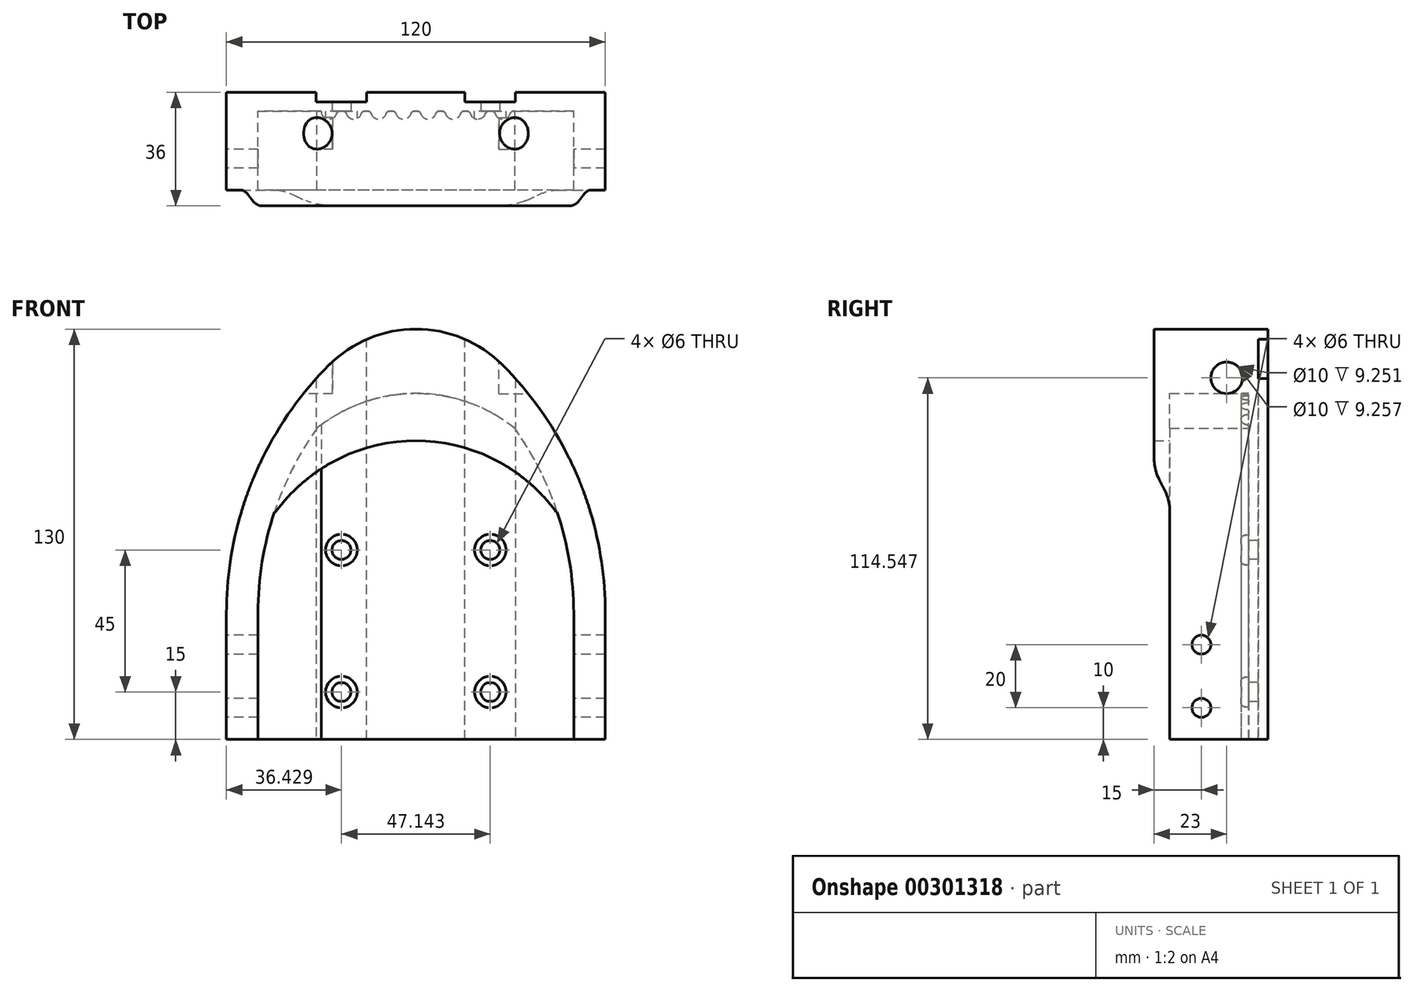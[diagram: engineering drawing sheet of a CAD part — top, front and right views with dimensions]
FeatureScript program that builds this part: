
annotation { "Feature Type Name" : "Feature", "Feature Type Description" : "" }
export const myFeature = defineFeature(function(context is Context, id is Id, definition is map)
    precondition{}
    {
        {
            var Q0;
            Q0=qCreatedBy(makeId("Front.planeOp"),FACE);
            var sketch = newSketch(context, id + "F0", { "sketchPlane" : qUnion([Q0])});
            skArc(sketch, "E0", {"start": v(-27.5, 118.6) * mm, "mid": v(-51.55, 82.52) * mm, "end": v(-60, 40) * mm});
            skArc(sketch, "E1", {"start": v(0, 130) * mm, "mid": v(-14.89, 127.03) * mm, "end": v(-27.5, 118.6) * mm});
            skLineSegment(sketch, "E2", {"start": v(-60, 0) * mm, "end": v(0, 0) * mm});
            skArc(sketch, "E3.MirrorCS", {"start": v(0, 130) * mm, "mid": v(14.89, 127.03) * mm, "end": v(27.5, 118.6) * mm});
            skArc(sketch, "E4.MirrorCS", {"start": v(27.5, 118.6) * mm, "mid": v(51.55, 82.52) * mm, "end": v(60, 40) * mm});
            skLineSegment(sketch, "E5.MirrorCS", {"start": v(60, 0) * mm, "end": v(0, 0) * mm});
            skLineSegment(sketch, "E6", {"start": v(-60, 40) * mm, "end": v(-60, 0) * mm});
            skLineSegment(sketch, "E7", {"start": v(60, 40) * mm, "end": v(60, 0) * mm});
            skSolve(sketch);
        }
        {
            var Q0;
            Q0=qSketchRegion(id+"F0",true);
            extrude(context, id + "F1", {"entities" : qUnion([Q0]), "depth" : 3 * mm});
        }
        {
            var Q0;
            Q0=makeQuery(id+"F1.opExtrude","CAP_FACE",FACE,{"disambiguationData":[OSD([sQuery(id+"F0.wireOp",EDGE,"E0"),sQuery(id+"F0.wireOp",EDGE,"E1"),sQuery(id+"F0.wireOp",EDGE,"E2"),sQuery(id+"F0.wireOp",EDGE,"E3.MirrorCS"),sQuery(id+"F0.wireOp",EDGE,"E4.MirrorCS"),sQuery(id+"F0.wireOp",EDGE,"E5.MirrorCS")])],"isStart":false});
            var sketch = newSketch(context, id + "F2", { "sketchPlane" : qUnion([Q0])});
            skArc(sketch, "E8", {"start": v(27.5, 118.6) * mm, "mid": v(0, 130) * mm, "end": v(-27.5, 118.6) * mm});
            skLineSegment(sketch, "E9", {"start": v(-27.5, 118.6) * mm, "end": v(-27.5, 118.6) * mm});
            skArc(sketch, "E10", {"start": v(0, 109.62) * mm, "mid": v(-16.6, 106.78) * mm, "end": v(-31.33, 98.6) * mm});
            skLineSegment(sketch, "E11", {"start": v(-50, 0) * mm, "end": v(-60, 0) * mm});
            skArc(sketch, "E12", {"start": v(-27.5, 118.6) * mm, "mid": v(-51.55, 82.52) * mm, "end": v(-60, 40) * mm});
            skLineSegment(sketch, "E13", {"start": v(-60, 40) * mm, "end": v(-60, 0) * mm});
            skLineSegment(sketch, "E14", {"start": v(-50, 0) * mm, "end": v(-50, 40) * mm});
            skArc(sketch, "E15", {"start": v(-31.33, 98.6) * mm, "mid": v(-45.22, 70.75) * mm, "end": v(-50, 40) * mm});
            skArc(sketch, "E16.MirrorCS", {"start": v(27.5, 118.6) * mm, "mid": v(51.55, 82.52) * mm, "end": v(60, 40) * mm});
            skLineSegment(sketch, "E17.MirrorCS", {"start": v(50, 0) * mm, "end": v(60, 0) * mm});
            skArc(sketch, "E18.MirrorCS", {"start": v(31.33, 98.6) * mm, "mid": v(45.22, 70.75) * mm, "end": v(50, 40) * mm});
            skLineSegment(sketch, "E19.MirrorCS", {"start": v(50, 0) * mm, "end": v(50, 40) * mm});
            skLineSegment(sketch, "E20.MirrorCS", {"start": v(60, 40) * mm, "end": v(60, 0) * mm});
            skArc(sketch, "E21.MirrorCS", {"start": v(0, 109.62) * mm, "mid": v(16.6, 106.78) * mm, "end": v(31.33, 98.6) * mm});
            skSolve(sketch);
        }
        {
            var Q0;
            Q0=qSketchRegion(id+"F2",true);
            extrude(context, id + "F3", {"entities" : qUnion([Q0]), "operationType" : NewBodyOperationType.ADD, "depth" : 25 * mm});
        }
        {
            var Q0;
            Q0=makeQuery(id+"F1.opExtrude","SWEPT_FACE",FACE,{"disambiguationData":[OSD([sQuery(id+"F0.wireOp",EDGE,"E2"),sQuery(id+"F0.wireOp",EDGE,"E5.MirrorCS")])]});
            var sketch = newSketch(context, id + "F4", { "sketchPlane" : qUnion([Q0])});
            skArc(sketch, "E22", {"start": v(30, 3) * mm, "mid": v(27.5, 5.5) * mm, "end": v(25, 3) * mm});
            skLineSegment(sketch, "E23", {"start": v(25, 3) * mm, "end": v(30, 3) * mm});
            skArc(sketch, "E24.1.0.0", {"start": v(22.14, 3) * mm, "mid": v(19.64, 5.5) * mm, "end": v(17.14, 3) * mm});
            skLineSegment(sketch, "E24.1.0.1", {"start": v(17.14, 3) * mm, "end": v(22.14, 3) * mm});
            skArc(sketch, "E24.2.0.0", {"start": v(14.29, 3) * mm, "mid": v(11.79, 5.5) * mm, "end": v(9.29, 3) * mm});
            skLineSegment(sketch, "E24.2.0.1", {"start": v(9.29, 3) * mm, "end": v(14.29, 3) * mm});
            skArc(sketch, "E24.3.0.0", {"start": v(6.43, 3) * mm, "mid": v(3.93, 5.5) * mm, "end": v(1.43, 3) * mm});
            skLineSegment(sketch, "E24.3.0.1", {"start": v(1.43, 3) * mm, "end": v(6.43, 3) * mm});
            skArc(sketch, "E24.4.0.0", {"start": v(-1.43, 3) * mm, "mid": v(-3.93, 5.5) * mm, "end": v(-6.43, 3) * mm});
            skLineSegment(sketch, "E24.4.0.1", {"start": v(-6.43, 3) * mm, "end": v(-1.43, 3) * mm});
            skArc(sketch, "E24.5.0.0", {"start": v(-9.29, 3) * mm, "mid": v(-11.79, 5.5) * mm, "end": v(-14.29, 3) * mm});
            skLineSegment(sketch, "E24.5.0.1", {"start": v(-14.29, 3) * mm, "end": v(-9.29, 3) * mm});
            skArc(sketch, "E24.6.0.0", {"start": v(-17.14, 3) * mm, "mid": v(-19.64, 5.5) * mm, "end": v(-22.14, 3) * mm});
            skLineSegment(sketch, "E24.6.0.1", {"start": v(-22.14, 3) * mm, "end": v(-17.14, 3) * mm});
            skArc(sketch, "E24.7.0.0", {"start": v(-25, 3) * mm, "mid": v(-27.5, 5.5) * mm, "end": v(-30, 3) * mm});
            skLineSegment(sketch, "E24.7.0.1", {"start": v(-30, 3) * mm, "end": v(-25, 3) * mm});
            skLineSegment(sketch, "E24.direction1", {"start": v(17.14, 3) * mm, "end": v(25, 3) * mm, "construction": true});
            skSolve(sketch);
        }
        {
            var Q0;
            Q0=qSketchRegion(id+"F4",true);
            extrude(context, id + "F5", {"entities" : qUnion([Q0]), "operationType" : NewBodyOperationType.ADD, "endBound" : BoundingType.UP_TO_NEXT, "oppositeDirection" : true, "depth" : 25 * mm});
        }
        {
            var Q0;
            {var subQ0=sQuery(id+"F4.wireOp",EDGE,"E23");var subQ1=sQuery(id+"F4.wireOp",EDGE,"E22");var subQ2=sQuery(id+"F0.wireOp",EDGE,"E5.MirrorCS");var subQ3=sQuery(id+"F0.wireOp",EDGE,"E2");Q0=makeQuery(id+"F5.opExtrude","SWEPT_EDGE",EDGE,{"disambiguationData":[OSD([subQ3,subQ2,subQ1,subQ0]),TDD([makeQuery(id+"F4.imprint","INTERSECT",VERTEX,{"disambiguationData":[OD(1.0)],"derivedFrom":[makeQuery(id+"F1.opExtrude","CAP_EDGE",EDGE,{"disambiguationData":[OSD([subQ3,subQ2])],"isStart":false}),subQ1,subQ0]})])]});}
            var Q1;
            {var subQ0=sQuery(id+"F4.wireOp",EDGE,"E23");var subQ1=sQuery(id+"F4.wireOp",EDGE,"E22");var subQ2=sQuery(id+"F0.wireOp",EDGE,"E5.MirrorCS");var subQ3=sQuery(id+"F0.wireOp",EDGE,"E2");Q1=makeQuery(id+"F5.opExtrude","SWEPT_EDGE",EDGE,{"disambiguationData":[OSD([subQ3,subQ2,subQ1,subQ0]),TDD([makeQuery(id+"F4.imprint","INTERSECT",VERTEX,{"disambiguationData":[OD(0.0)],"derivedFrom":[makeQuery(id+"F1.opExtrude","CAP_EDGE",EDGE,{"disambiguationData":[OSD([subQ3,subQ2])],"isStart":false}),subQ1,subQ0]})])]});}
            var Q2;
            {var subQ0=sQuery(id+"F4.wireOp",EDGE,"E24.1.0.1");var subQ1=sQuery(id+"F4.wireOp",EDGE,"E24.1.0.0");var subQ2=sQuery(id+"F0.wireOp",EDGE,"E5.MirrorCS");var subQ3=sQuery(id+"F0.wireOp",EDGE,"E2");Q2=makeQuery(id+"F5.opExtrude","SWEPT_EDGE",EDGE,{"disambiguationData":[OSD([subQ3,subQ2,subQ1,subQ0]),TDD([makeQuery(id+"F4.imprint","INTERSECT",VERTEX,{"disambiguationData":[OD(0.0)],"derivedFrom":[makeQuery(id+"F1.opExtrude","CAP_EDGE",EDGE,{"disambiguationData":[OSD([subQ3,subQ2])],"isStart":false}),subQ1,subQ0]})])]});}
            var Q3;
            {var subQ0=sQuery(id+"F4.wireOp",EDGE,"E24.2.0.1");var subQ1=sQuery(id+"F4.wireOp",EDGE,"E24.2.0.0");var subQ2=sQuery(id+"F0.wireOp",EDGE,"E5.MirrorCS");var subQ3=sQuery(id+"F0.wireOp",EDGE,"E2");Q3=makeQuery(id+"F5.opExtrude","SWEPT_EDGE",EDGE,{"disambiguationData":[OSD([subQ3,subQ2,subQ1,subQ0]),TDD([makeQuery(id+"F4.imprint","INTERSECT",VERTEX,{"disambiguationData":[OD(0.0)],"derivedFrom":[makeQuery(id+"F1.opExtrude","CAP_EDGE",EDGE,{"disambiguationData":[OSD([subQ3,subQ2])],"isStart":false}),subQ1,subQ0]})])]});}
            var Q4;
            {var subQ0=sQuery(id+"F4.wireOp",EDGE,"E24.3.0.1");var subQ1=sQuery(id+"F4.wireOp",EDGE,"E24.3.0.0");var subQ2=sQuery(id+"F0.wireOp",EDGE,"E5.MirrorCS");var subQ3=sQuery(id+"F0.wireOp",EDGE,"E2");Q4=makeQuery(id+"F5.opExtrude","SWEPT_EDGE",EDGE,{"disambiguationData":[OSD([subQ3,subQ2,subQ1,subQ0]),TDD([makeQuery(id+"F4.imprint","INTERSECT",VERTEX,{"disambiguationData":[OD(0.0)],"derivedFrom":[makeQuery(id+"F1.opExtrude","CAP_EDGE",EDGE,{"disambiguationData":[OSD([subQ3,subQ2])],"isStart":false}),subQ1,subQ0]})])]});}
            var Q5;
            {var subQ0=sQuery(id+"F4.wireOp",EDGE,"E24.4.0.1");var subQ1=sQuery(id+"F4.wireOp",EDGE,"E24.4.0.0");var subQ2=sQuery(id+"F0.wireOp",EDGE,"E5.MirrorCS");var subQ3=sQuery(id+"F0.wireOp",EDGE,"E2");Q5=makeQuery(id+"F5.opExtrude","SWEPT_EDGE",EDGE,{"disambiguationData":[OSD([subQ3,subQ2,subQ1,subQ0]),TDD([makeQuery(id+"F4.imprint","INTERSECT",VERTEX,{"disambiguationData":[OD(0.0)],"derivedFrom":[makeQuery(id+"F1.opExtrude","CAP_EDGE",EDGE,{"disambiguationData":[OSD([subQ3,subQ2])],"isStart":false}),subQ1,subQ0]})])]});}
            var Q6;
            {var subQ0=sQuery(id+"F4.wireOp",EDGE,"E24.5.0.1");var subQ1=sQuery(id+"F4.wireOp",EDGE,"E24.5.0.0");var subQ2=sQuery(id+"F0.wireOp",EDGE,"E5.MirrorCS");var subQ3=sQuery(id+"F0.wireOp",EDGE,"E2");Q6=makeQuery(id+"F5.opExtrude","SWEPT_EDGE",EDGE,{"disambiguationData":[OSD([subQ3,subQ2,subQ1,subQ0]),TDD([makeQuery(id+"F4.imprint","INTERSECT",VERTEX,{"disambiguationData":[OD(0.0)],"derivedFrom":[makeQuery(id+"F1.opExtrude","CAP_EDGE",EDGE,{"disambiguationData":[OSD([subQ3,subQ2])],"isStart":false}),subQ1,subQ0]})])]});}
            var Q7;
            {var subQ0=sQuery(id+"F4.wireOp",EDGE,"E24.6.0.1");var subQ1=sQuery(id+"F4.wireOp",EDGE,"E24.6.0.0");var subQ2=sQuery(id+"F0.wireOp",EDGE,"E5.MirrorCS");var subQ3=sQuery(id+"F0.wireOp",EDGE,"E2");Q7=makeQuery(id+"F5.opExtrude","SWEPT_EDGE",EDGE,{"disambiguationData":[OSD([subQ3,subQ2,subQ1,subQ0]),TDD([makeQuery(id+"F4.imprint","INTERSECT",VERTEX,{"disambiguationData":[OD(0.0)],"derivedFrom":[makeQuery(id+"F1.opExtrude","CAP_EDGE",EDGE,{"disambiguationData":[OSD([subQ3,subQ2])],"isStart":false}),subQ1,subQ0]})])]});}
            var Q8;
            {var subQ0=sQuery(id+"F4.wireOp",EDGE,"E24.7.0.1");var subQ1=sQuery(id+"F4.wireOp",EDGE,"E24.7.0.0");var subQ2=sQuery(id+"F0.wireOp",EDGE,"E5.MirrorCS");var subQ3=sQuery(id+"F0.wireOp",EDGE,"E2");Q8=makeQuery(id+"F5.opExtrude","SWEPT_EDGE",EDGE,{"disambiguationData":[OSD([subQ3,subQ2,subQ1,subQ0]),TDD([makeQuery(id+"F4.imprint","INTERSECT",VERTEX,{"disambiguationData":[OD(0.0)],"derivedFrom":[makeQuery(id+"F1.opExtrude","CAP_EDGE",EDGE,{"disambiguationData":[OSD([subQ3,subQ2])],"isStart":false}),subQ1,subQ0]})])]});}
            var Q9;
            {var subQ0=sQuery(id+"F4.wireOp",EDGE,"E24.8.0.1");var subQ1=sQuery(id+"F4.wireOp",EDGE,"E24.8.0.0");var subQ2=sQuery(id+"F0.wireOp",EDGE,"E5.MirrorCS");var subQ3=sQuery(id+"F0.wireOp",EDGE,"E2");Q9=makeQuery(id+"F5.opExtrude","SWEPT_EDGE",EDGE,{"disambiguationData":[OSD([subQ3,subQ2,subQ1,subQ0]),TDD([makeQuery(id+"F4.imprint","INTERSECT",VERTEX,{"disambiguationData":[OD(0.0)],"derivedFrom":[makeQuery(id+"F1.opExtrude","CAP_EDGE",EDGE,{"disambiguationData":[OSD([subQ3,subQ2])],"isStart":false}),subQ1,subQ0]})])]});}
            var Q10;
            {var subQ0=sQuery(id+"F4.wireOp",EDGE,"E24.9.0.1");var subQ1=sQuery(id+"F4.wireOp",EDGE,"E24.9.0.0");var subQ2=sQuery(id+"F0.wireOp",EDGE,"E5.MirrorCS");var subQ3=sQuery(id+"F0.wireOp",EDGE,"E2");Q10=makeQuery(id+"F5.opExtrude","SWEPT_EDGE",EDGE,{"disambiguationData":[OSD([subQ3,subQ2,subQ1,subQ0]),TDD([makeQuery(id+"F4.imprint","INTERSECT",VERTEX,{"disambiguationData":[OD(0.0)],"derivedFrom":[makeQuery(id+"F1.opExtrude","CAP_EDGE",EDGE,{"disambiguationData":[OSD([subQ3,subQ2])],"isStart":false}),subQ1,subQ0]})])]});}
            var Q11;
            {var subQ0=sQuery(id+"F4.wireOp",EDGE,"E24.1.0.1");var subQ1=sQuery(id+"F4.wireOp",EDGE,"E24.1.0.0");var subQ2=sQuery(id+"F0.wireOp",EDGE,"E5.MirrorCS");var subQ3=sQuery(id+"F0.wireOp",EDGE,"E2");Q11=makeQuery(id+"F5.opExtrude","SWEPT_EDGE",EDGE,{"disambiguationData":[OSD([subQ3,subQ2,subQ1,subQ0]),TDD([makeQuery(id+"F4.imprint","INTERSECT",VERTEX,{"disambiguationData":[OD(1.0)],"derivedFrom":[makeQuery(id+"F1.opExtrude","CAP_EDGE",EDGE,{"disambiguationData":[OSD([subQ3,subQ2])],"isStart":false}),subQ1,subQ0]})])]});}
            var Q12;
            {var subQ0=sQuery(id+"F4.wireOp",EDGE,"E24.2.0.1");var subQ1=sQuery(id+"F4.wireOp",EDGE,"E24.2.0.0");var subQ2=sQuery(id+"F0.wireOp",EDGE,"E5.MirrorCS");var subQ3=sQuery(id+"F0.wireOp",EDGE,"E2");Q12=makeQuery(id+"F5.opExtrude","SWEPT_EDGE",EDGE,{"disambiguationData":[OSD([subQ3,subQ2,subQ1,subQ0]),TDD([makeQuery(id+"F4.imprint","INTERSECT",VERTEX,{"disambiguationData":[OD(1.0)],"derivedFrom":[makeQuery(id+"F1.opExtrude","CAP_EDGE",EDGE,{"disambiguationData":[OSD([subQ3,subQ2])],"isStart":false}),subQ1,subQ0]})])]});}
            var Q13;
            {var subQ0=sQuery(id+"F4.wireOp",EDGE,"E24.3.0.1");var subQ1=sQuery(id+"F4.wireOp",EDGE,"E24.3.0.0");var subQ2=sQuery(id+"F0.wireOp",EDGE,"E5.MirrorCS");var subQ3=sQuery(id+"F0.wireOp",EDGE,"E2");Q13=makeQuery(id+"F5.opExtrude","SWEPT_EDGE",EDGE,{"disambiguationData":[OSD([subQ3,subQ2,subQ1,subQ0]),TDD([makeQuery(id+"F4.imprint","INTERSECT",VERTEX,{"disambiguationData":[OD(1.0)],"derivedFrom":[makeQuery(id+"F1.opExtrude","CAP_EDGE",EDGE,{"disambiguationData":[OSD([subQ3,subQ2])],"isStart":false}),subQ1,subQ0]})])]});}
            var Q14;
            {var subQ0=sQuery(id+"F4.wireOp",EDGE,"E24.4.0.1");var subQ1=sQuery(id+"F4.wireOp",EDGE,"E24.4.0.0");var subQ2=sQuery(id+"F0.wireOp",EDGE,"E5.MirrorCS");var subQ3=sQuery(id+"F0.wireOp",EDGE,"E2");Q14=makeQuery(id+"F5.opExtrude","SWEPT_EDGE",EDGE,{"disambiguationData":[OSD([subQ3,subQ2,subQ1,subQ0]),TDD([makeQuery(id+"F4.imprint","INTERSECT",VERTEX,{"disambiguationData":[OD(1.0)],"derivedFrom":[makeQuery(id+"F1.opExtrude","CAP_EDGE",EDGE,{"disambiguationData":[OSD([subQ3,subQ2])],"isStart":false}),subQ1,subQ0]})])]});}
            var Q15;
            {var subQ0=sQuery(id+"F4.wireOp",EDGE,"E24.5.0.1");var subQ1=sQuery(id+"F4.wireOp",EDGE,"E24.5.0.0");var subQ2=sQuery(id+"F0.wireOp",EDGE,"E5.MirrorCS");var subQ3=sQuery(id+"F0.wireOp",EDGE,"E2");Q15=makeQuery(id+"F5.opExtrude","SWEPT_EDGE",EDGE,{"disambiguationData":[OSD([subQ3,subQ2,subQ1,subQ0]),TDD([makeQuery(id+"F4.imprint","INTERSECT",VERTEX,{"disambiguationData":[OD(1.0)],"derivedFrom":[makeQuery(id+"F1.opExtrude","CAP_EDGE",EDGE,{"disambiguationData":[OSD([subQ3,subQ2])],"isStart":false}),subQ1,subQ0]})])]});}
            var Q16;
            {var subQ0=sQuery(id+"F4.wireOp",EDGE,"E24.6.0.1");var subQ1=sQuery(id+"F4.wireOp",EDGE,"E24.6.0.0");var subQ2=sQuery(id+"F0.wireOp",EDGE,"E5.MirrorCS");var subQ3=sQuery(id+"F0.wireOp",EDGE,"E2");Q16=makeQuery(id+"F5.opExtrude","SWEPT_EDGE",EDGE,{"disambiguationData":[OSD([subQ3,subQ2,subQ1,subQ0]),TDD([makeQuery(id+"F4.imprint","INTERSECT",VERTEX,{"disambiguationData":[OD(1.0)],"derivedFrom":[makeQuery(id+"F1.opExtrude","CAP_EDGE",EDGE,{"disambiguationData":[OSD([subQ3,subQ2])],"isStart":false}),subQ1,subQ0]})])]});}
            var Q17;
            {var subQ0=sQuery(id+"F4.wireOp",EDGE,"E24.7.0.1");var subQ1=sQuery(id+"F4.wireOp",EDGE,"E24.7.0.0");var subQ2=sQuery(id+"F0.wireOp",EDGE,"E5.MirrorCS");var subQ3=sQuery(id+"F0.wireOp",EDGE,"E2");Q17=makeQuery(id+"F5.opExtrude","SWEPT_EDGE",EDGE,{"disambiguationData":[OSD([subQ3,subQ2,subQ1,subQ0]),TDD([makeQuery(id+"F4.imprint","INTERSECT",VERTEX,{"disambiguationData":[OD(1.0)],"derivedFrom":[makeQuery(id+"F1.opExtrude","CAP_EDGE",EDGE,{"disambiguationData":[OSD([subQ3,subQ2])],"isStart":false}),subQ1,subQ0]})])]});}
            var Q18;
            {var subQ0=sQuery(id+"F4.wireOp",EDGE,"E24.8.0.1");var subQ1=sQuery(id+"F4.wireOp",EDGE,"E24.8.0.0");var subQ2=sQuery(id+"F0.wireOp",EDGE,"E5.MirrorCS");var subQ3=sQuery(id+"F0.wireOp",EDGE,"E2");Q18=makeQuery(id+"F5.opExtrude","SWEPT_EDGE",EDGE,{"disambiguationData":[OSD([subQ3,subQ2,subQ1,subQ0]),TDD([makeQuery(id+"F4.imprint","INTERSECT",VERTEX,{"disambiguationData":[OD(1.0)],"derivedFrom":[makeQuery(id+"F1.opExtrude","CAP_EDGE",EDGE,{"disambiguationData":[OSD([subQ3,subQ2])],"isStart":false}),subQ1,subQ0]})])]});}
            var Q19;
            {var subQ0=sQuery(id+"F4.wireOp",EDGE,"E24.9.0.1");var subQ1=sQuery(id+"F4.wireOp",EDGE,"E24.9.0.0");var subQ2=sQuery(id+"F0.wireOp",EDGE,"E5.MirrorCS");var subQ3=sQuery(id+"F0.wireOp",EDGE,"E2");Q19=makeQuery(id+"F5.opExtrude","SWEPT_EDGE",EDGE,{"disambiguationData":[OSD([subQ3,subQ2,subQ1,subQ0]),TDD([makeQuery(id+"F4.imprint","INTERSECT",VERTEX,{"disambiguationData":[OD(1.0)],"derivedFrom":[makeQuery(id+"F1.opExtrude","CAP_EDGE",EDGE,{"disambiguationData":[OSD([subQ3,subQ2])],"isStart":false}),subQ1,subQ0]})])]});}
            fillet(context, id + "F6", {"entities" : qUnion([Q0, Q1, Q2, Q3, Q4, Q5, Q6, Q7, Q8, Q9, Q10, Q11, Q12, Q13, Q14, Q15, Q16, Q17, Q18, Q19]), "radius" : 1 * mm, "tangentPropagation" : true, "allowEdgeOverflow" : false});
        }
        {
            var Q0;
            Q0=makeQuery(id+"F3.opExtrude","CAP_FACE",FACE,{"disambiguationData":[OSD([sQuery(id+"F2.wireOp",EDGE,"E8"),sQuery(id+"F2.wireOp",EDGE,"E9"),sQuery(id+"F2.wireOp",EDGE,"K2G1USgo-3m0U-XLTb-5Cc7-swm9MIo1nxKb"),sQuery(id+"F2.wireOp",EDGE,"E10"),sQuery(id+"F2.wireOp",EDGE,"fCSB4vCm-hjBn-03hI-EFcb-PruF7x6NOwHa"),sQuery(id+"F2.wireOp",EDGE,"JiTlebmn-TQbH-jICJ-myWO-59kou3JwVklX"),sQuery(id+"F2.wireOp",EDGE,"KOVmWARr-3AFX-fmdh-qVK6-FX16uVcEkwG9"),sQuery(id+"F2.wireOp",EDGE,"RxoCjrL7-CFMo-3ynv-jpnN-dJrFagMQBz5N")])],"isStart":false});
            var sketch = newSketch(context, id + "F7", { "sketchPlane" : qUnion([Q0])});
            skPoint(sketch, "E25", {"position": v(-31.34, 114.55) * mm});
            skPoint(sketch, "E26", {"position": v(31.34, 114.55) * mm});
            skSolve(sketch);
        }
        {
            var Q0;
            Q0=qCreatedBy(makeId("Right.planeOp"),FACE);
            cPlane(context, id + "F8", {"entities" : qUnion([Q0]), "cplaneType" : CPlaneType.OFFSET, "offset" : (62.67 / 2) * mm, "width" : 150 * mm, "height" : 150 * mm});
        }
        {
            var Q0;
            Q0=qCreatedBy(makeId("Right.planeOp"),FACE);
            cPlane(context, id + "F9", {"entities" : qUnion([Q0]), "cplaneType" : CPlaneType.OFFSET, "offset" : (62.67 / 2) * mm, "oppositeDirection" : true, "width" : 150 * mm, "height" : 150 * mm});
        }
        {
            var Q0;
            Q0=qCreatedBy(id+"F8.planeOp",FACE);
            var sketch = newSketch(context, id + "F10", { "sketchPlane" : qUnion([Q0])});
            skCircle(sketch, "E27", {"center": v(-10, 114.55) * mm, "radius": 5 * mm});
            skSolve(sketch);
        }
        {
            var Q0;
            Q0=qSketchRegion(id+"F10",true);
            extrude(context, id + "F11", {"entities" : qUnion([Q0]), "operationType" : NewBodyOperationType.REMOVE, "oppositeDirection" : true, "depth" : 5 * mm, "hasSecondDirection" : true, "secondDirectionOppositeDirection" : false, "secondDirectionDepth" : 25 * mm});
        }
        {
            var Q0;
            Q0=qCreatedBy(id+"F9.planeOp",FACE);
            var sketch = newSketch(context, id + "F12", { "sketchPlane" : qUnion([Q0])});
            skCircle(sketch, "E28", {"center": v(-10, 114.55) * mm, "radius": 5 * mm});
            skSolve(sketch);
        }
        {
            var Q0;
            Q0=qSketchRegion(id+"F12",true);
            extrude(context, id + "F13", {"entities" : qUnion([Q0]), "operationType" : NewBodyOperationType.REMOVE, "depth" : 5 * mm, "hasSecondDirection" : true, "secondDirectionOppositeDirection" : true, "secondDirectionDepth" : 25 * mm});
        }
        {
            var Q0;
            {var subQ0=makeQuery(id+"F5.opExtrude","CAP_FACE",FACE,{"disambiguationData":[OSD([sQuery(id+"F4.wireOp",EDGE,"E24.5.0.0"),sQuery(id+"F4.wireOp",EDGE,"E24.5.0.1")])],"isStart":true});var subQ1=sQuery(id+"F0.wireOp",EDGE,"E5.MirrorCS");var subQ2=sQuery(id+"F0.wireOp",EDGE,"E2");var subQ3=makeQuery(id+"F1.opExtrude","SWEPT_FACE",FACE,{"disambiguationData":[OSD([subQ2,subQ1])]});var subQ4=sQuery(id+"F4.wireOp",EDGE,"E24.3.0.0");var subQ5=makeQuery(id+"F5.opExtrude","CAP_FACE",FACE,{"disambiguationData":[OSD([subQ4,sQuery(id+"F4.wireOp",EDGE,"E24.3.0.1")])],"isStart":true});var subQ6=sQuery(id+"F4.wireOp",EDGE,"E24.2.0.0");var subQ7=makeQuery(id+"F5.opExtrude","CAP_FACE",FACE,{"disambiguationData":[OSD([subQ6,sQuery(id+"F4.wireOp",EDGE,"E24.2.0.1")])],"isStart":true});var subQ8=makeQuery(id+"F5.opExtrude","SWEPT_FACE",FACE,{"disambiguationData":[OSD([subQ6])]});var subQ9=sQuery(id+"F4.wireOp",EDGE,"E24.1.0.0");var subQ10=makeQuery(id+"F5.opExtrude","CAP_FACE",FACE,{"disambiguationData":[OSD([subQ9,sQuery(id+"F4.wireOp",EDGE,"E24.1.0.1")])],"isStart":true});var subQ11=makeQuery(id+"F5.opExtrude","CAP_FACE",FACE,{"disambiguationData":[OSD([sQuery(id+"F4.wireOp",EDGE,"E24.4.0.0"),sQuery(id+"F4.wireOp",EDGE,"E24.4.0.1")])],"isStart":true});var subQ12=makeQuery(id+"F3.opExtrude","SWEPT_FACE",FACE,{"disambiguationData":[OSD([sQuery(id+"F2.wireOp",EDGE,"E10")])]});var subQ13=sQuery(id+"F4.wireOp",EDGE,"E22");var subQ14=makeQuery(id+"F5.opExtrude","CAP_FACE",FACE,{"disambiguationData":[OSD([subQ13,sQuery(id+"F4.wireOp",EDGE,"E23")])],"isStart":true});var subQ15=makeQuery(id+"F5.opExtrude","CAP_FACE",FACE,{"disambiguationData":[OSD([sQuery(id+"F4.wireOp",EDGE,"E24.6.0.0"),sQuery(id+"F4.wireOp",EDGE,"E24.6.0.1")])],"isStart":true});var subQ16=makeQuery(id+"F5.opExtrude","CAP_FACE",FACE,{"disambiguationData":[OSD([sQuery(id+"F4.wireOp",EDGE,"E24.7.0.0"),sQuery(id+"F4.wireOp",EDGE,"E24.7.0.1")])],"isStart":true});var subQ17=makeQuery(id+"F5.opExtrude","CAP_FACE",FACE,{"disambiguationData":[OSD([sQuery(id+"F4.wireOp",EDGE,"E24.8.0.0"),sQuery(id+"F4.wireOp",EDGE,"E24.8.0.1")])],"isStart":true});var subQ18=makeQuery(id+"F5.opExtrude","CAP_FACE",FACE,{"disambiguationData":[OSD([sQuery(id+"F4.wireOp",EDGE,"E24.9.0.0"),sQuery(id+"F4.wireOp",EDGE,"E24.9.0.1")])],"isStart":true});var subQ19=makeQuery(id+"F1.opExtrude","CAP_FACE",FACE,{"disambiguationData":[OSD([sQuery(id+"F0.wireOp",EDGE,"E0"),sQuery(id+"F0.wireOp",EDGE,"E1"),subQ2,sQuery(id+"F0.wireOp",EDGE,"E3.MirrorCS"),sQuery(id+"F0.wireOp",EDGE,"E4.MirrorCS"),subQ1])],"isStart":false});var subQ20=makeQuery(id+"F5.opExtrude","SWEPT_FACE",FACE,{"disambiguationData":[OSD([subQ9])]});Q0=makeQuery(id+"FagDk5R1PXxC9WP_1.boolean.opBoolean","MERGE",FACE,{"derivedFrom":[makeQuery(id+"F5.boolean.opBoolean","SPLIT",FACE,{"disambiguationData":[TD([subQ3,subQ12,makeQuery(id+"F5.opExtrude","SWEPT_FACE",FACE,{"disambiguationData":[OSD([subQ13])]}),subQ14,subQ20,subQ10,subQ7,subQ5,subQ11,subQ0,subQ15,subQ16,subQ17,subQ18])],"derivedFrom":subQ19}),makeQuery(id+"F5.boolean.opBoolean","SPLIT",FACE,{"disambiguationData":[TD([subQ3,subQ12,subQ14,subQ20,subQ10,subQ8,subQ7,subQ5,subQ11,subQ0,subQ15,subQ16,subQ17,subQ18])],"derivedFrom":subQ19}),makeQuery(id+"F5.boolean.opBoolean","SPLIT",FACE,{"disambiguationData":[TD([subQ3,subQ12,subQ14,subQ10,subQ8,subQ7,makeQuery(id+"F5.opExtrude","SWEPT_FACE",FACE,{"disambiguationData":[OSD([subQ4])]}),subQ5,subQ11,subQ0,subQ15,subQ16,subQ17,subQ18])],"derivedFrom":subQ19}),makeQuery(id+"FagDk5R1PXxC9WP_1.opExtrude","SWEPT_FACE",FACE,{"disambiguationData":[OSD([sQuery(id+"FtMZI0YXXD80vIJ_1.wireOp",EDGE,"6BlepP5m-DG3n-HtGD-IaAT-YB7duayLEJRe.bottom")])]})]});}
            var sketch = newSketch(context, id + "F14", { "sketchPlane" : qUnion([Q0])});
            skCircle(sketch, "E29", {"center": v(23.57, 15) * mm, "radius": 3 * mm});
            skPoint(sketch, "E29.centerSnap0", {"position": v(23.57, 0) * mm});
            skCircle(sketch, "E30", {"center": v(23.57, 60) * mm, "radius": 3 * mm});
            skCircle(sketch, "E31.MirrorC", {"center": v(-23.57, 15) * mm, "radius": 3 * mm});
            skCircle(sketch, "E32.MirrorC", {"center": v(-23.57, 60) * mm, "radius": 3 * mm});
            skPoint(sketch, "E33", {"position": v(0, 0) * mm});
            skSolve(sketch);
        }
        {
            var Q0;
            Q0=qSketchRegion(id+"F14",true);
            extrude(context, id + "F15", {"entities" : qUnion([Q0]), "operationType" : NewBodyOperationType.REMOVE, "oppositeDirection" : true, "depth" : 25 * mm});
        }
        {
            var Q0;
            {var subQ0=sQuery(id+"F4.wireOp",EDGE,"E22");var subQ1=makeQuery(id+"F3.opExtrude","SWEPT_FACE",FACE,{"disambiguationData":[OSD([sQuery(id+"F2.wireOp",EDGE,"fCSB4vCm-hjBn-03hI-EFcb-PruF7x6NOwHa")])]});var subQ2=makeQuery(id+"F3.opExtrude","SWEPT_FACE",FACE,{"disambiguationData":[OSD([sQuery(id+"F2.wireOp",EDGE,"E9")])]});var subQ3=sQuery(id+"F0.wireOp",EDGE,"E5.MirrorCS");var subQ4=sQuery(id+"F0.wireOp",EDGE,"E2");var subQ5=sQuery(id+"F0.wireOp",EDGE,"E0");var subQ6=makeQuery(id+"F1.opExtrude","CAP_FACE",FACE,{"disambiguationData":[OSD([subQ5,sQuery(id+"F0.wireOp",EDGE,"E1"),subQ4,sQuery(id+"F0.wireOp",EDGE,"E3.MirrorCS"),sQuery(id+"F0.wireOp",EDGE,"E4.MirrorCS"),subQ3])],"isStart":false});var subQ7=makeQuery(id+"F1.opExtrude","SWEPT_FACE",FACE,{"disambiguationData":[OSD([subQ5])]});Q0=makeQuery(id+"F5.boolean.opBoolean","SPLIT",FACE,{"disambiguationData":[TD([subQ7,makeQuery(id+"F1.opExtrude","SWEPT_FACE",FACE,{"disambiguationData":[OSD([subQ4,subQ3])]}),subQ2,subQ1,makeQuery(id+"FEmyDYQQVgRQXe1_1.boolean.opBoolean","COPY",FACE,{"disambiguationData":[TD([subQ7])],"derivedFrom":makeQuery(id+"FEmyDYQQVgRQXe1_1.opExtrude","SWEPT_FACE",FACE,{"disambiguationData":[OSD([sQuery(id+"F95mhF6FaMZOlkV_1.wireOp",EDGE,"16wo293t-KL3b-4ck3-VDR1-H0NEiYk0Jyv5")])]})}),makeQuery(id+"F5.opExtrude","SWEPT_FACE",FACE,{"disambiguationData":[OSD([subQ0])]}),makeQuery(id+"F5.opExtrude","CAP_FACE",FACE,{"disambiguationData":[OSD([subQ0,sQuery(id+"F4.wireOp",EDGE,"E23")])],"isStart":true}),makeQuery(id+"F5.opExtrude","CAP_FACE",FACE,{"disambiguationData":[OSD([sQuery(id+"F4.wireOp",EDGE,"E24.1.0.0"),sQuery(id+"F4.wireOp",EDGE,"E24.1.0.1")])],"isStart":true}),makeQuery(id+"F5.opExtrude","CAP_FACE",FACE,{"disambiguationData":[OSD([sQuery(id+"F4.wireOp",EDGE,"E24.2.0.0"),sQuery(id+"F4.wireOp",EDGE,"E24.2.0.1")])],"isStart":true}),makeQuery(id+"F5.opExtrude","CAP_FACE",FACE,{"disambiguationData":[OSD([sQuery(id+"F4.wireOp",EDGE,"E24.3.0.0"),sQuery(id+"F4.wireOp",EDGE,"E24.3.0.1")])],"isStart":true}),makeQuery(id+"F5.opExtrude","CAP_FACE",FACE,{"disambiguationData":[OSD([sQuery(id+"F4.wireOp",EDGE,"E24.4.0.0"),sQuery(id+"F4.wireOp",EDGE,"E24.4.0.1")])],"isStart":true}),makeQuery(id+"F5.opExtrude","CAP_FACE",FACE,{"disambiguationData":[OSD([sQuery(id+"F4.wireOp",EDGE,"E24.5.0.0"),sQuery(id+"F4.wireOp",EDGE,"E24.5.0.1")])],"isStart":true}),makeQuery(id+"F5.opExtrude","CAP_FACE",FACE,{"disambiguationData":[OSD([sQuery(id+"F4.wireOp",EDGE,"E24.6.0.0"),sQuery(id+"F4.wireOp",EDGE,"E24.6.0.1")])],"isStart":true}),makeQuery(id+"F5.opExtrude","CAP_FACE",FACE,{"disambiguationData":[OSD([sQuery(id+"F4.wireOp",EDGE,"E24.7.0.0"),sQuery(id+"F4.wireOp",EDGE,"E24.7.0.1")])],"isStart":true}),makeQuery(id+"F5.opExtrude","CAP_FACE",FACE,{"disambiguationData":[OSD([sQuery(id+"F4.wireOp",EDGE,"E24.8.0.0"),sQuery(id+"F4.wireOp",EDGE,"E24.8.0.1")])],"isStart":true}),makeQuery(id+"F5.opExtrude","CAP_FACE",FACE,{"disambiguationData":[OSD([sQuery(id+"F4.wireOp",EDGE,"E24.9.0.0"),sQuery(id+"F4.wireOp",EDGE,"E24.9.0.1")])],"isStart":true})])],"derivedFrom":subQ6});}
            var sketch = newSketch(context, id + "F16", { "sketchPlane" : qUnion([Q0])});
            skCircle(sketch, "E34", {"center": v(-23.57, 60) * mm, "radius": 5 * mm});
            skCircle(sketch, "E35", {"center": v(23.57, 60) * mm, "radius": 5 * mm});
            skCircle(sketch, "E36", {"center": v(23.57, 15) * mm, "radius": 5 * mm});
            skCircle(sketch, "E37", {"center": v(-23.57, 15) * mm, "radius": 5 * mm});
            skSolve(sketch);
        }
        {
            var Q0;
            Q0=qSketchRegion(id+"F16",true);
            extrude(context, id + "F17", {"entities" : qUnion([Q0]), "operationType" : NewBodyOperationType.REMOVE, "depth" : 25 * mm});
        }
        {
            var Q0;
            Q0=makeQuery(id+"F1.opExtrude","CAP_FACE",FACE,{"disambiguationData":[OSD([sQuery(id+"F0.wireOp",EDGE,"E0"),sQuery(id+"F0.wireOp",EDGE,"E1"),sQuery(id+"F0.wireOp",EDGE,"E2"),sQuery(id+"F0.wireOp",EDGE,"E3.MirrorCS"),sQuery(id+"F0.wireOp",EDGE,"E4.MirrorCS"),sQuery(id+"F0.wireOp",EDGE,"E5.MirrorCS")])],"isStart":true});
            var sketch = newSketch(context, id + "F18", { "sketchPlane" : qUnion([Q0])});
            skPoint(sketch, "E38", {"position": v(-23.57, 15) * mm});
            skPoint(sketch, "E39", {"position": v(23.57, 15) * mm});
            skLineSegment(sketch, "E40", {"start": v(-31.57, 114.29) * mm, "end": v(-31.57, 0) * mm});
            skLineSegment(sketch, "E41", {"start": v(-31.57, 0) * mm, "end": v(-60, 0) * mm});
            skLineSegment(sketch, "E42", {"start": v(-60, 0) * mm, "end": v(-60, 40) * mm});
            skArc(sketch, "E43", {"start": v(-31.57, 114.29) * mm, "mid": v(-52.65, 79.77) * mm, "end": v(-60, 40) * mm});
            skLineSegment(sketch, "E44", {"start": v(0, 0) * mm, "end": v(-15.57, 0) * mm});
            skLineSegment(sketch, "E45", {"start": v(-15.57, 0) * mm, "end": v(-15.57, 126.74) * mm});
            skLineSegment(sketch, "E46.MirrorCS", {"start": v(0, 0) * mm, "end": v(15.57, 0) * mm});
            skLineSegment(sketch, "E47.MirrorCS", {"start": v(31.57, 0) * mm, "end": v(60, 0) * mm});
            skLineSegment(sketch, "E48.MirrorCS", {"start": v(31.57, 114.29) * mm, "end": v(31.57, 0) * mm});
            skLineSegment(sketch, "E49.MirrorCS", {"start": v(15.57, 0) * mm, "end": v(15.57, 126.74) * mm});
            skArc(sketch, "E50.MirrorCS", {"start": v(31.57, 114.29) * mm, "mid": v(52.65, 79.77) * mm, "end": v(60, 40) * mm});
            skLineSegment(sketch, "E51.MirrorCS", {"start": v(60, 0) * mm, "end": v(60, 40) * mm});
            skArc(sketch, "E52", {"start": v(15.57, 126.74) * mm, "mid": v(0, 130) * mm, "end": v(-15.57, 126.74) * mm});
            skSolve(sketch);
        }
        {
            var Q0;
            Q0=qSketchRegion(id+"F18",true);
            extrude(context, id + "F19", {"entities" : qUnion([Q0]), "operationType" : NewBodyOperationType.ADD, "depth" : 3 * mm});
        }
        {
            var Q0;
            Q0=makeQuery(id+"F3.opExtrude","CAP_FACE",FACE,{"disambiguationData":[OSD([sQuery(id+"F2.wireOp",EDGE,"E8"),sQuery(id+"F2.wireOp",EDGE,"E9"),sQuery(id+"F2.wireOp",EDGE,"K2G1USgo-3m0U-XLTb-5Cc7-swm9MIo1nxKb"),sQuery(id+"F2.wireOp",EDGE,"E10"),sQuery(id+"F2.wireOp",EDGE,"fCSB4vCm-hjBn-03hI-EFcb-PruF7x6NOwHa"),sQuery(id+"F2.wireOp",EDGE,"JiTlebmn-TQbH-jICJ-myWO-59kou3JwVklX"),sQuery(id+"F2.wireOp",EDGE,"KOVmWARr-3AFX-fmdh-qVK6-FX16uVcEkwG9"),sQuery(id+"F2.wireOp",EDGE,"RxoCjrL7-CFMo-3ynv-jpnN-dJrFagMQBz5N")])],"isStart":false});
            var sketch = newSketch(context, id + "F20", { "sketchPlane" : qUnion([Q0])});
            skLineSegment(sketch, "E53", {"start": v(-27.5, 118.6) * mm, "end": v(-27.5, 118.6) * mm});
            skArc(sketch, "E54", {"start": v(-27.5, 118.6) * mm, "mid": v(-44.52, 96.6) * mm, "end": v(-55.57, 71.1) * mm});
            skPoint(sketch, "E55", {"position": v(0, 109.62) * mm});
            skArc(sketch, "E56", {"start": v(27.5, 118.6) * mm, "mid": v(0, 130) * mm, "end": v(-27.5, 118.6) * mm});
            skLineSegment(sketch, "E57", {"start": v(-55.57, 71.1) * mm, "end": v(-45.1, 71.1) * mm});
            skLineSegment(sketch, "E58", {"start": v(55.57, 71.1) * mm, "end": v(45.1, 71.1) * mm});
            skArc(sketch, "E59", {"start": v(45.1, 71.1) * mm, "mid": v(0, 94.62) * mm, "end": v(-45.1, 71.1) * mm});
            skPoint(sketch, "E60", {"position": v(0, 94.62) * mm});
            skArc(sketch, "E61", {"start": v(55.57, 71.1) * mm, "mid": v(44.52, 96.6) * mm, "end": v(27.5, 118.6) * mm});
            skSolve(sketch);
        }
        {
            var Q0;
            Q0=qSketchRegion(id+"F20",true);
            extrude(context, id + "F21", {"entities" : qUnion([Q0]), "operationType" : NewBodyOperationType.ADD, "depth" : 5 * mm});
        }
        {
            var Q0;
            Q0=qCreatedBy(makeId("Right.planeOp"),FACE);
            var sketch = newSketch(context, id + "F22", { "sketchPlane" : qUnion([Q0])});
            skLineSegment(sketch, "E62", {"start": v(-29.65, 78.92) * mm, "end": v(-31.35, 82.26) * mm});
            skLineSegment(sketch, "E63", {"start": v(-33, 89.1) * mm, "end": v(-33, 92.98) * mm});
            skLineSegment(sketch, "E64", {"start": v(-33, 92.98) * mm, "end": v(-39.66, 92.98) * mm});
            skLineSegment(sketch, "E65", {"start": v(-39.66, 92.98) * mm, "end": v(-39.66, 71.1) * mm});
            skLineSegment(sketch, "E66", {"start": v(-39.66, 71.1) * mm, "end": v(-28, 71.1) * mm});
            skLineSegment(sketch, "E67", {"start": v(-28, 71.1) * mm, "end": v(-28, 72.1) * mm});
            skPoint(sketch, "E68.visualSharp", {"position": v(-28, 75.7) * mm});
            skArc(sketch, "E68.filletArc", {"start": v(-28, 72.1) * mm, "mid": v(-28.42, 75.6) * mm, "end": v(-29.65, 78.92) * mm});
            skPoint(sketch, "E69.visualSharp", {"position": v(-33, 85.47) * mm});
            skArc(sketch, "E69.filletArc", {"start": v(-33, 89.1) * mm, "mid": v(-32.58, 85.57) * mm, "end": v(-31.35, 82.26) * mm});
            skSolve(sketch);
        }
        {
            var Q0;
            Q0=qSketchRegion(id+"F22",true);
            extrude(context, id + "F23", {"entities" : qUnion([Q0]), "operationType" : NewBodyOperationType.REMOVE, "endBound" : BoundingType.THROUGH_ALL, "oppositeDirection" : true, "depth" : 25 * mm, "hasSecondDirection" : true, "secondDirectionBound" : SecondDirectionBoundingType.THROUGH_ALL, "secondDirectionOppositeDirection" : false, "secondDirectionDepth" : 25 * mm});
        }
        {
            var Q0;
            Q0=makeQuery(id+"F19.boolean.opBoolean","MERGE",FACE,{"derivedFrom":[makeQuery(id+"F3.boolean.opBoolean","MERGE",FACE,{"derivedFrom":[makeQuery(id+"F1.opExtrude","SWEPT_FACE",FACE,{"disambiguationData":[OSD([sQuery(id+"F0.wireOp",EDGE,"E6")])]}),makeQuery(id+"F3.opExtrude","SWEPT_FACE",FACE,{"disambiguationData":[OSD([sQuery(id+"F2.wireOp",EDGE,"E13")])]})]}),makeQuery(id+"F19.opExtrude","SWEPT_FACE",FACE,{"disambiguationData":[OSD([sQuery(id+"F18.wireOp",EDGE,"E51.MirrorCS")])]})]});
            var sketch = newSketch(context, id + "F24", { "sketchPlane" : qUnion([Q0])});
            skCircle(sketch, "E70", {"center": v(18, 10) * mm, "radius": 3 * mm});
            skCircle(sketch, "E71", {"center": v(18, 30) * mm, "radius": 3 * mm});
            skLineSegment(sketch, "E72", {"start": v(28, 0) * mm, "end": v(28, 20) * mm});
            skLineSegment(sketch, "E73", {"start": v(28, 40) * mm, "end": v(28, 20) * mm});
            skPoint(sketch, "E74", {"position": v(28, 30) * mm});
            skPoint(sketch, "E75", {"position": v(28, 10) * mm});
            skSolve(sketch);
        }
        {
            var Q0;
            Q0 = qSketchRegion(id + "F24", true);
            extrude(context, id + "F25", {"entities" : qUnion([Q0]), "operationType" : NewBodyOperationType.REMOVE, "endBound" : BoundingType.THROUGH_ALL, "oppositeDirection" : true, "depth" : 25 * mm});
        }
    });
